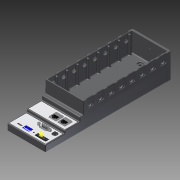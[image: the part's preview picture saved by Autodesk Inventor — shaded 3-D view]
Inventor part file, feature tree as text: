
AUTODESK INVENTOR PART (.ipt)
format: ipt  version: 2011 (Build 150239000, 239)  size: 13,086,720 bytes
history: native  units: mm
features: plane x12, other x9, imported_body x1, pattern_linear x1
ambient origin geometry x8: Origin, YZ Plane, XZ Plane, XY Plane, X Axis, Y Axis, Z Axis, Center Point
bodies: Solid1 (feature_tree)
feature tree (23):
  imported_body  "Base1"
  plane  "Work Plane4"
  pattern_linear  "Rectangular Pattern1"  Count1=8 Spacing1=0.0mm
  other  "Work Point5"
  other  "Work Point6"
  other  "Work Point7"
  other  "Work Point8"
  other  "Work Axis1"
  plane  "Work Plane5"
  plane  "Work Plane6"
  plane  "Work Plane7"
  plane  "Work Plane8"
  plane  "Work Plane9"
  plane  "Work Plane10"
  plane  "Work Plane11"
  plane  "Work Plane16"
  other  "Work Axis4"
  plane  "Work Plane17"
  other  "Work Axis5"
  plane  "Work Plane18"
  other  "Work Axis6"
  plane  "Work Plane19"
  other  "Work Axis7"
